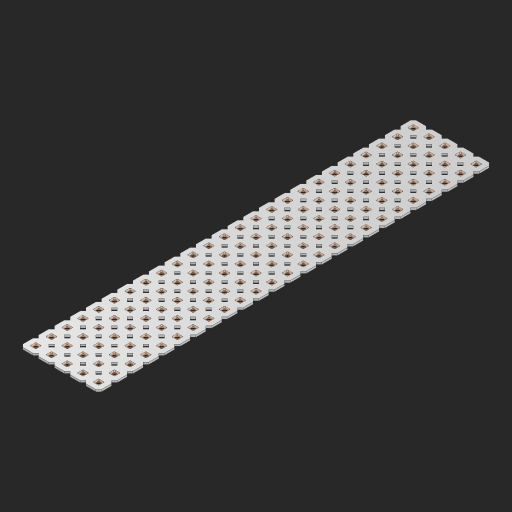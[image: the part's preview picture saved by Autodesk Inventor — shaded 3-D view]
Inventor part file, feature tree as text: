
AUTODESK INVENTOR PART (.ipt)
format: ipt  version: 2023 (Build 270158000, 158)  size: 1,723,904 bytes
history: native  units: in
note: dims shown in document units (in); Inventor stores cm internally (conversion verified against a paired STEP export)
features: other x126, extrude x124, sketch x2, pattern_linear x1
ambient origin geometry x8: Origin, YZ Plane, XZ Plane, XY Plane, X Axis, Y Axis, Z Axis, Center Point
bodies: Solid1 (feature_tree), Body (feature_tree)
feature tree (253):
  pattern_linear  "Rectangular Pattern1"  Spacing1=0.09in  [1 undecoded]
  sketch  "Sketch1"  dims[d1=0.5in]
  sketch  "Sketch2"  dims[d2=0.182in d3=0.09in d4=0.09in d5=0.09in d6=0.09in d7=0.09in d8=0.09in d9=0.09in d10=0.09in d11=0.02in d13=0.0in d14=0.172in d15=0.0625in d16=0.0in d19=0.5in d22=0.5in]
  other  "Srf1"
  other  "Srf126"
  other  "Srf127"
  other  "Srf128"
  other  "Srf129"
  other  "Srf130"
  other  "Srf131"
  other  "Srf250"
  other  "Srf251"
  other  "Srf252"
  other  "Srf253"
  other  "Srf254"
  other  "Srf255"
  other  "Srf256"
  other  "Srf257"
  other  "Srf258"
  other  "Srf259"
  other  "Srf260"
  other  "Srf261"
  other  "Srf262"
  other  "Srf263"
  other  "Srf264"
  other  "Srf265"
  other  "Srf266"
  other  "Srf267"
  other  "Srf268"
  other  "Srf269"
  other  "Srf270"
  other  "Srf271"
  other  "Srf272"
  other  "Srf273"
  other  "Srf274"
  other  "Srf275"
  other  "Srf276"
  other  "Srf277"
  other  "Srf278"
  other  "Srf279"
  other  "Srf280"
  other  "Srf281"
  other  "Srf282"
  other  "Srf283"
  other  "Srf284"
  other  "Srf285"
  other  "Srf286"
  other  "Srf287"
  other  "Srf288"
  other  "Srf289"
  other  "Srf290"
  other  "Srf291"
  other  "Srf292"
  other  "Srf293"
  other  "Srf294"
  other  "Srf295"
  other  "Srf296"
  other  "Srf297"
  other  "Srf298"
  other  "Srf299"
  other  "Srf300"
  other  "Srf301"
  other  "Srf302"
  other  "Srf303"
  other  "Srf304"
  other  "Srf305"
  other  "Srf306"
  other  "Srf307"
  other  "Srf308"
  other  "Srf309"
  other  "Srf310"
  other  "Srf311"
  other  "Srf312"
  other  "Srf313"
  other  "Srf314"
  other  "Srf315"
  other  "Srf316"
  other  "Srf317"
  other  "Srf318"
  other  "Srf319"
  other  "Srf320"
  other  "Srf321"
  other  "Srf322"
  other  "Srf323"
  other  "Srf324"
  other  "Srf325"
  other  "Srf326"
  other  "Srf327"
  other  "Srf328"
  other  "Srf329"
  other  "Srf330"
  other  "Srf331"
  other  "Srf332"
  other  "Srf333"
  other  "Srf334"
  other  "Srf335"
  other  "Srf336"
  other  "Srf337"
  other  "Srf338"
  other  "Srf339"
  other  "Srf340"
  other  "Srf341"
  other  "Srf342"
  other  "Srf343"
  other  "Srf344"
  other  "Srf345"
  other  "Srf346"
  other  "Srf347"
  other  "Srf348"
  other  "Srf349"
  other  "Srf350"
  other  "Srf351"
  other  "Srf352"
  other  "Srf353"
  other  "Srf354"
  other  "Srf355"
  other  "Srf356"
  other  "Srf357"
  other  "Srf358"
  other  "Srf359"
  other  "Srf360"
  other  "Srf361"
  other  "Srf362"
  other  "Srf363"
  other  "Srf364"
  other  "Srf365"
  other  "Srf366"
  other  "Srf367"
  other  "Circle"
  extrude  "ExtrusionSrf126"  Depth=0.09in
  extrude  "ExtrusionSrf127"  Depth=0.09in
  extrude  "ExtrusionSrf128"  Depth=0.09in
  extrude  "ExtrusionSrf129"  Depth=0.09in
  extrude  "ExtrusionSrf130"  Depth=0.09in
  extrude  "ExtrusionSrf131"  Depth=0.09in
  extrude  "ExtrusionSrf250"  Depth=0.09in
  extrude  "ExtrusionSrf251"  Depth=0.02in
  extrude  "ExtrusionSrf252"  TaperAngle=0.0deg  [1 undecoded]
  extrude  "ExtrusionSrf253"  Depth=0.5in
  extrude  "ExtrusionSrf254"  Depth=0.0625in TaperAngle=0.0deg
  extrude  "ExtrusionSrf255"  Depth=0.5in
  extrude  "ExtrusionSrf256"  Depth=0.5in
  extrude  "ExtrusionSrf257"  [1 undecoded]
  extrude  "ExtrusionSrf258"  [1 undecoded]
  extrude  "ExtrusionSrf259"  [1 undecoded]
  extrude  "ExtrusionSrf260"  [1 undecoded]
  extrude  "ExtrusionSrf261"  [1 undecoded]
  extrude  "ExtrusionSrf262"  [1 undecoded]
  extrude  "ExtrusionSrf263"  [1 undecoded]
  extrude  "ExtrusionSrf264"  [1 undecoded]
  extrude  "ExtrusionSrf265"  [1 undecoded]
  extrude  "ExtrusionSrf266"  [1 undecoded]
  extrude  "ExtrusionSrf267"  [1 undecoded]
  extrude  "ExtrusionSrf268"  [1 undecoded]
  extrude  "ExtrusionSrf269"  [1 undecoded]
  extrude  "ExtrusionSrf270"  [1 undecoded]
  extrude  "ExtrusionSrf271"  [1 undecoded]
  extrude  "ExtrusionSrf272"  [1 undecoded]
  extrude  "ExtrusionSrf273"  [1 undecoded]
  extrude  "ExtrusionSrf274"  [1 undecoded]
  extrude  "ExtrusionSrf275"  [1 undecoded]
  extrude  "ExtrusionSrf276"  [1 undecoded]
  extrude  "ExtrusionSrf277"  [1 undecoded]
  extrude  "ExtrusionSrf278"  [1 undecoded]
  extrude  "ExtrusionSrf279"  [1 undecoded]
  extrude  "ExtrusionSrf280"  [1 undecoded]
  extrude  "ExtrusionSrf281"  [1 undecoded]
  extrude  "ExtrusionSrf282"  [1 undecoded]
  extrude  "ExtrusionSrf283"  [1 undecoded]
  extrude  "ExtrusionSrf284"  [1 undecoded]
  extrude  "ExtrusionSrf285"  [1 undecoded]
  extrude  "ExtrusionSrf286"  [1 undecoded]
  extrude  "ExtrusionSrf287"  [1 undecoded]
  extrude  "ExtrusionSrf288"  [1 undecoded]
  extrude  "ExtrusionSrf289"  [1 undecoded]
  extrude  "ExtrusionSrf290"  [1 undecoded]
  extrude  "ExtrusionSrf291"  [1 undecoded]
  extrude  "ExtrusionSrf292"  [1 undecoded]
  extrude  "ExtrusionSrf293"  [1 undecoded]
  extrude  "ExtrusionSrf294"  [1 undecoded]
  extrude  "ExtrusionSrf295"  [1 undecoded]
  extrude  "ExtrusionSrf296"  [1 undecoded]
  extrude  "ExtrusionSrf297"  [1 undecoded]
  extrude  "ExtrusionSrf298"  [1 undecoded]
  extrude  "ExtrusionSrf299"  [1 undecoded]
  extrude  "ExtrusionSrf300"  [1 undecoded]
  extrude  "ExtrusionSrf301"  [1 undecoded]
  extrude  "ExtrusionSrf302"  [1 undecoded]
  extrude  "ExtrusionSrf303"  [1 undecoded]
  extrude  "ExtrusionSrf304"  [1 undecoded]
  extrude  "ExtrusionSrf305"  [1 undecoded]
  extrude  "ExtrusionSrf306"  [1 undecoded]
  extrude  "ExtrusionSrf307"  [1 undecoded]
  extrude  "ExtrusionSrf308"  [1 undecoded]
  extrude  "ExtrusionSrf309"  [1 undecoded]
  extrude  "ExtrusionSrf310"  [1 undecoded]
  extrude  "ExtrusionSrf311"  [1 undecoded]
  extrude  "ExtrusionSrf312"  [1 undecoded]
  extrude  "ExtrusionSrf313"  [1 undecoded]
  extrude  "ExtrusionSrf314"  [1 undecoded]
  extrude  "ExtrusionSrf315"  [1 undecoded]
  extrude  "ExtrusionSrf316"  [1 undecoded]
  extrude  "ExtrusionSrf317"  [1 undecoded]
  extrude  "ExtrusionSrf318"  [1 undecoded]
  extrude  "ExtrusionSrf319"  [1 undecoded]
  extrude  "ExtrusionSrf320"  [1 undecoded]
  extrude  "ExtrusionSrf321"  [1 undecoded]
  extrude  "ExtrusionSrf322"  [1 undecoded]
  extrude  "ExtrusionSrf323"  [1 undecoded]
  extrude  "ExtrusionSrf324"  [1 undecoded]
  extrude  "ExtrusionSrf325"  [1 undecoded]
  extrude  "ExtrusionSrf326"  [1 undecoded]
  extrude  "ExtrusionSrf327"  [1 undecoded]
  extrude  "ExtrusionSrf328"  [1 undecoded]
  extrude  "ExtrusionSrf329"  [1 undecoded]
  extrude  "ExtrusionSrf330"  [1 undecoded]
  extrude  "ExtrusionSrf331"  [1 undecoded]
  extrude  "ExtrusionSrf332"  [1 undecoded]
  extrude  "ExtrusionSrf333"  [1 undecoded]
  extrude  "ExtrusionSrf334"  [1 undecoded]
  extrude  "ExtrusionSrf335"  [1 undecoded]
  extrude  "ExtrusionSrf336"  [1 undecoded]
  extrude  "ExtrusionSrf337"  [1 undecoded]
  extrude  "ExtrusionSrf338"  [1 undecoded]
  extrude  "ExtrusionSrf339"  [1 undecoded]
  extrude  "ExtrusionSrf340"  [1 undecoded]
  extrude  "ExtrusionSrf341"  [1 undecoded]
  extrude  "ExtrusionSrf342"  [1 undecoded]
  extrude  "ExtrusionSrf343"  [1 undecoded]
  extrude  "ExtrusionSrf344"  [1 undecoded]
  extrude  "ExtrusionSrf345"  [1 undecoded]
  extrude  "ExtrusionSrf346"  [1 undecoded]
  extrude  "ExtrusionSrf347"  [1 undecoded]
  extrude  "ExtrusionSrf348"  [1 undecoded]
  extrude  "ExtrusionSrf349"  [1 undecoded]
  extrude  "ExtrusionSrf350"  [1 undecoded]
  extrude  "ExtrusionSrf351"  [1 undecoded]
  extrude  "ExtrusionSrf352"  [1 undecoded]
  extrude  "ExtrusionSrf353"  [1 undecoded]
  extrude  "ExtrusionSrf354"  [1 undecoded]
  extrude  "ExtrusionSrf355"  [1 undecoded]
  extrude  "ExtrusionSrf356"  [1 undecoded]
  extrude  "ExtrusionSrf357"  [1 undecoded]
  extrude  "ExtrusionSrf358"  [1 undecoded]
  extrude  "ExtrusionSrf359"  [1 undecoded]
  extrude  "ExtrusionSrf360"  [1 undecoded]
  extrude  "ExtrusionSrf361"  [1 undecoded]
  extrude  "ExtrusionSrf362"  [1 undecoded]
  extrude  "ExtrusionSrf363"  [1 undecoded]
  extrude  "ExtrusionSrf364"  [1 undecoded]
  extrude  "ExtrusionSrf365"  [1 undecoded]
  extrude  "ExtrusionSrf366"  [1 undecoded]
  extrude  "ExtrusionSrf367"  [1 undecoded]
note: 113 required parameter values undecoded (feature->parameter linkage not recoverable at this tier; creation-order binding heuristic only, values carry confidence <= 0.55)
